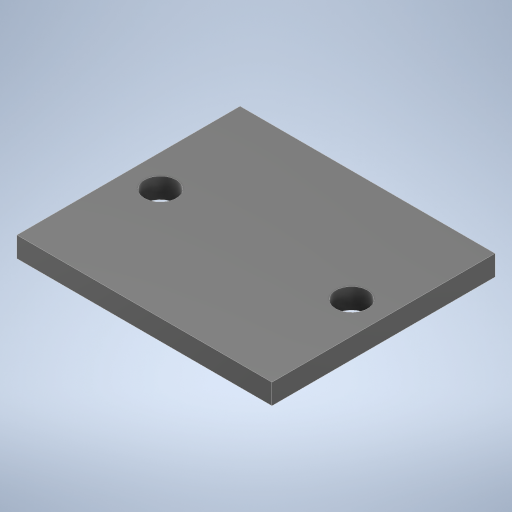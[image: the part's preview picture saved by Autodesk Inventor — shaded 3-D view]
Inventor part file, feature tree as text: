
AUTODESK INVENTOR PART (.ipt)
format: ipt  version: 2024.2 (Build 282272000, 272)  size: 223,744 bytes
history: native  units: mm
features: sketch x1, extrude x1, hole x1
ambient origin geometry x8: Origin, YZ Plane, XZ Plane, XY Plane, X Axis, Y Axis, Z Axis, Center Point
bodies: Solid1 (feature_tree)
feature tree (3):
  sketch  "Sketch1"  dims[d0=17.5mm d1=20.0mm d7=1.6mm d8=0.0mm d10=2.5mm d11=4.0mm d12=4.0mm d13=2.0mm d14=90.0deg d15=8.0mm d16=20.594885mm d19=15.0mm]
  extrude  "Extrusion1"  Depth=20.0mm
  hole  "Phi2.5"  [1 undecoded]
note: 1 required parameter value undecoded (feature->parameter linkage not recoverable at this tier; creation-order binding heuristic only, values carry confidence <= 0.55)
